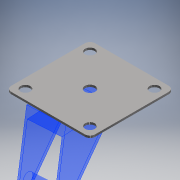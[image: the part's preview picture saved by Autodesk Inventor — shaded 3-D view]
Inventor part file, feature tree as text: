
AUTODESK INVENTOR PART (.ipt)
format: ipt  version: 2019 (Build 230136000, 136)  size: 128,512 bytes
history: native  units: mm
features: other x1, extrude x1, sketch x1
ambient origin geometry x8: Origin, YZ Plane, XZ Plane, XY Plane, X Axis, Y Axis, Z Axis, Center Point
bodies: Body1 (feature_tree)
feature tree (3):
  other  "솔리드1"
  extrude  "돌출1"  Depth=82.0mm
  sketch  "스케치1"
